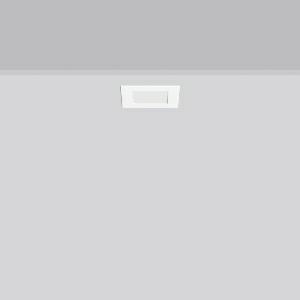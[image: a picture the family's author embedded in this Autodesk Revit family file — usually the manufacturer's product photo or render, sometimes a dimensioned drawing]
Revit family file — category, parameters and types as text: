
# Revit family: toledo_flat_square_e_901485_002_1_41f9
name_source: partatom
category: Lighting Fixtures
units: mm (PartAtom-declared; Revit-internal decimal feet)

## family parameters
Cut with Voids When Loaded = No
Host = Face
Light Source = No
Part Type = Normal
Room Calculation Point = No
Round Connector Dimension = Use Diameter
Shared = No

## types (1)
- TOLEDO FLAT square E (1 x LED Modul 840, 430 lm, 4000)
    Apparent Load = 5 VA
    CIE Flux Codes = 49 80 96 100 100
    Color Rendering = 80
    Color Temperature = 4000
    Default Elevation = 1800 mm
    Description = Series: TOLEDO FLAT square
Ultra thin recessed downlight. Housing: die-cast aluminium. Light guide and diffuser made of non-yellowing PMMA, opal matt. Ceiling installation with spring system. Mounting depth depends on ceiling strength. Suitable for through-wiring with separately available accessories. Surface mounted housing as accessory for all sizes. Retrofittable decorative cylinders made of chintz fabric as accessory, optional with satin finish plastic diffuser. Through-wiring box (5 pole) available as accessory. 
Colour: white
Length: 110 mm
Width: 110 mm
Height: 3 mm
Cut-out length: 96 mm
Cut-out width: 96 mm
Recess height: 27-56 mm
Luminaire: recess height: 31-51 mm
Lamp: LED
Socket: without socket
Colour temperature: 4000K
Colour rendering index (CRI): 80
System power: 5 W
Rated luminous flux: 430 lm
Luminous efficiency: 86 lm/W
Control gear: Regulated power supply
Protection class: II
Type of protection: IP 54
    Height = 0 mm  [stored 0 ft]
    Lamp = 1 x LED Modul 840
    Lamp Light Flux = 430 lm
    Lamp count = 1
    Length = 110 mm
    Lifetime = 50000 h
    Luminous efficacy = 86 lm/W
    Manufacturer = RZB
    ModVariant = No
    Model = 901485.002.1
    Mounting Place = Ceiling
    Mounting Type = Recessed
    Number of Poles = 1
    OnlyDefault = Yes
    Power Factor = 1
    Product Name = TOLEDO FLAT square E
    Product group = Recessed downlights
    ProductGroupID = 402
    Protection Class = Protection class II
    Protection Degree = IP 20
    RLX_Detail_Level = 1
    RLX_Emergency_Light_Flux = 0 lm
    RLX_Emergency_Type = 0
    RLX_Emergency_Type_DB = No
    RlxData = <blob elided: 57497 chars, md5=27d3d2dd>
    Socket = socket
    Standby Power = 0 W
    System Light Flux = 430 lm
    System Power = 5 W
    Type Comments = Product without accessories
    Type Image = 901485.002.jpg
    URL = http://relux.com
    VarID = ---
    Voltage = 230 V
    Voltage Range = 220-240 V
    Weight = 0.00 kg
    Width = 110 mm

note: [stored X ft] marks values corroborated as IEEE doubles in the binary element streams (Revit-internal decimal feet)

## geometry (parser evidence)
native form markers: Blend x4, Sweep x11
no freeform markers — native parametric forms only
